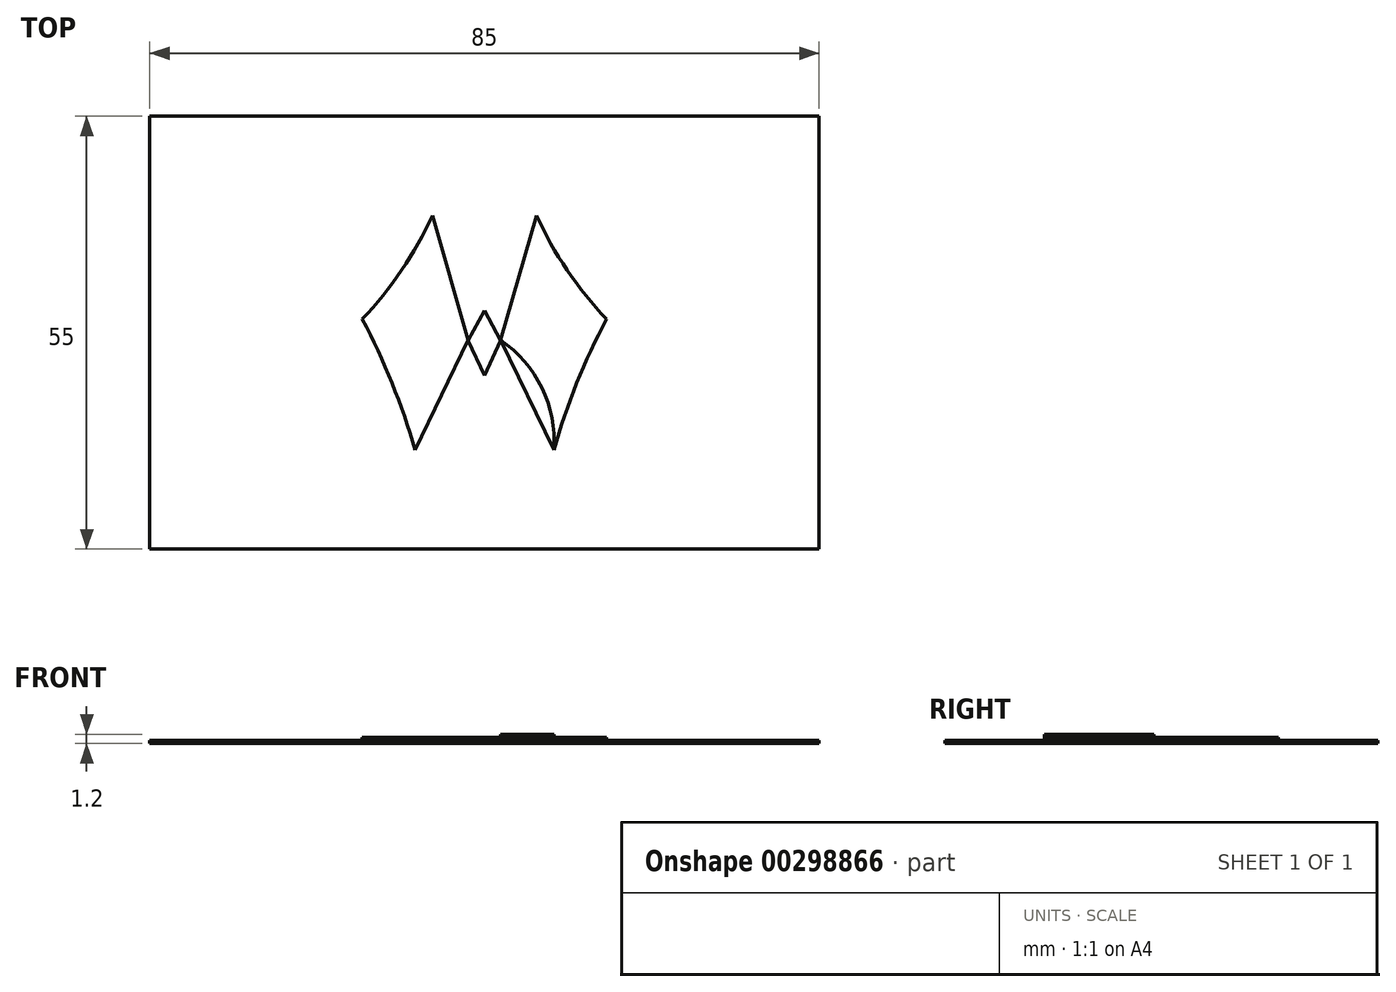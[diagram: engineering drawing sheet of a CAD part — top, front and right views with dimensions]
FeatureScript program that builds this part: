
annotation { "Feature Type Name" : "Feature", "Feature Type Description" : "" }
export const myFeature = defineFeature(function(context is Context, id is Id, definition is map)
    precondition{}
    {
        {
            var Q0;
            Q0=qCreatedBy(makeId("Top.planeOp"),FACE);
            var sketch = newSketch(context, id + "F0", { "sketchPlane" : qUnion([Q0])});
            skLineSegment(sketch, "E0", {"start": v(0, -5.43) * mm, "end": v(2.06, -1.02) * mm});
            skLineSegment(sketch, "E1", {"start": v(2.06, -1.02) * mm, "end": v(0, 2.85) * mm});
            skLineSegment(sketch, "E2", {"start": v(6.62, 14.87) * mm, "end": v(2.06, -0.95) * mm});
            skLineSegment(sketch, "E3", {"start": v(2.06, -0.95) * mm, "end": v(8.82, -14.87) * mm});
            skArc(sketch, "E4", {"start": v(15.52, 1.73) * mm, "mid": v(11.73, -6.4) * mm, "end": v(8.82, -14.87) * mm});
            skArc(sketch, "E5", {"start": v(6.62, 14.87) * mm, "mid": v(10.53, 7.93) * mm, "end": v(15.52, 1.73) * mm});
            skLineSegment(sketch, "E6.MirrorCS", {"start": v(-6.62, 14.87) * mm, "end": v(-2.06, -0.95) * mm});
            skLineSegment(sketch, "E7.MirrorCS", {"start": v(-2.06, -0.95) * mm, "end": v(-8.82, -14.87) * mm});
            skArc(sketch, "E8.MirrorCS", {"start": v(-15.52, 1.73) * mm, "mid": v(-11.73, -6.4) * mm, "end": v(-8.82, -14.87) * mm});
            skArc(sketch, "E9.MirrorCS", {"start": v(-6.62, 14.87) * mm, "mid": v(-10.53, 7.93) * mm, "end": v(-15.52, 1.73) * mm});
            skLineSegment(sketch, "E10.MirrorCS", {"start": v(-2.06, -1.02) * mm, "end": v(0, 2.85) * mm});
            skLineSegment(sketch, "E11.MirrorCS", {"start": v(0, -5.43) * mm, "end": v(-2.06, -1.02) * mm});
            skSolve(sketch);
        }
        {
            var Q0;
            Q0 = qSketchRegion(id + "F0", true);
            extrude(context, id + "F1", {"entities" : qUnion([Q0]), "depth" : 0.4 * mm});
        }
        {
            var Q0;
            Q0=qCreatedBy(makeId("Top.planeOp"),FACE);
            var sketch = newSketch(context, id + "F2", { "sketchPlane" : qUnion([Q0])});
            skLineSegment(sketch, "E12.bottom", {"start": v(-42.5, 27.5) * mm, "end": v(42.5, 27.5) * mm});
            skLineSegment(sketch, "E12.top", {"start": v(-42.5, -27.5) * mm, "end": v(42.5, -27.5) * mm});
            skLineSegment(sketch, "E12.left", {"start": v(-42.5, 27.5) * mm, "end": v(-42.5, -27.5) * mm});
            skLineSegment(sketch, "E12.right", {"start": v(42.5, 27.5) * mm, "end": v(42.5, -27.5) * mm});
            skSolve(sketch);
        }
        {
            var Q0;
            Q0 = qSketchRegion(id + "F2", true);
            extrude(context, id + "F3", {"entities" : qUnion([Q0]), "oppositeDirection" : true, "depth" : 0.4 * mm});
        }
        {
            var Q0;
            Q0=makeQuery(id+"F1.opExtrude","CAP_FACE",FACE,{"disambiguationData":[OSD([sQuery(id+"F0.wireOp",EDGE,"E2"),sQuery(id+"F0.wireOp",EDGE,"E3"),sQuery(id+"F0.wireOp",EDGE,"E4"),sQuery(id+"F0.wireOp",EDGE,"E5")])],"isStart":false});
            var sketch = newSketch(context, id + "F4", { "sketchPlane" : qUnion([Q0])});
            skLineSegment(sketch, "E13.0", {"start": v(-2.06, -0.95) * mm, "end": v(-6.62, 14.87) * mm});
            skLineSegment(sketch, "E13.1", {"start": v(-8.82, -14.87) * mm, "end": v(-2.06, -0.95) * mm});
            skArc(sketch, "E13.2", {"start": v(-15.52, 1.73) * mm, "mid": v(-11.73, -6.4) * mm, "end": v(-8.82, -14.87) * mm});
            skArc(sketch, "E13.3", {"start": v(-6.62, 14.87) * mm, "mid": v(-10.53, 7.93) * mm, "end": v(-15.52, 1.73) * mm});
            skArc(sketch, "E14", {"start": v(-6.62, 14.87) * mm, "mid": v(-6.4, 6.37) * mm, "end": v(-2.06, -0.95) * mm});
            skArc(sketch, "E15", {"start": v(-2.06, -0.95) * mm, "mid": v(-7.3, -7) * mm, "end": v(-8.82, -14.87) * mm});
            skArc(sketch, "E16.MirrorCS", {"start": v(2.06, -0.95) * mm, "mid": v(7.3, -7) * mm, "end": v(8.82, -14.87) * mm});
            skArc(sketch, "E17.MirrorCS", {"start": v(15.52, 1.73) * mm, "mid": v(11.73, -6.4) * mm, "end": v(8.82, -14.87) * mm});
            skArc(sketch, "E18.MirrorCS", {"start": v(6.62, 14.87) * mm, "mid": v(10.53, 7.93) * mm, "end": v(15.52, 1.73) * mm});
            skArc(sketch, "E19.MirrorCS", {"start": v(6.62, 14.87) * mm, "mid": v(6.4, 6.37) * mm, "end": v(2.06, -0.95) * mm});
            skSolve(sketch);
        }
        {
            var Q0;
            Q0=makeQuery(id+"F4.imprint","IMPRINT",FACE,{"disambiguationData":[TD([[makeQuery(id+"F4.imprint","IMPRINT",EDGE,{"derivedFrom":sQuery(id+"F4.wireOp",EDGE,"E13.2")}),1.0]])]});
            var Q1;
            Q1=makeQuery(id+"F4.imprint","IMPRINT",FACE,{"disambiguationData":[TD([[makeQuery(id+"F4.imprint","IMPRINT",EDGE,{"derivedFrom":sQuery(id+"F4.wireOp",EDGE,"E16.MirrorCS")}),1.0]])]});
            extrude(context, id + "F5", {"entities" : qUnion([Q0, Q1]), "depth" : 0.4 * mm});
        }
    });
